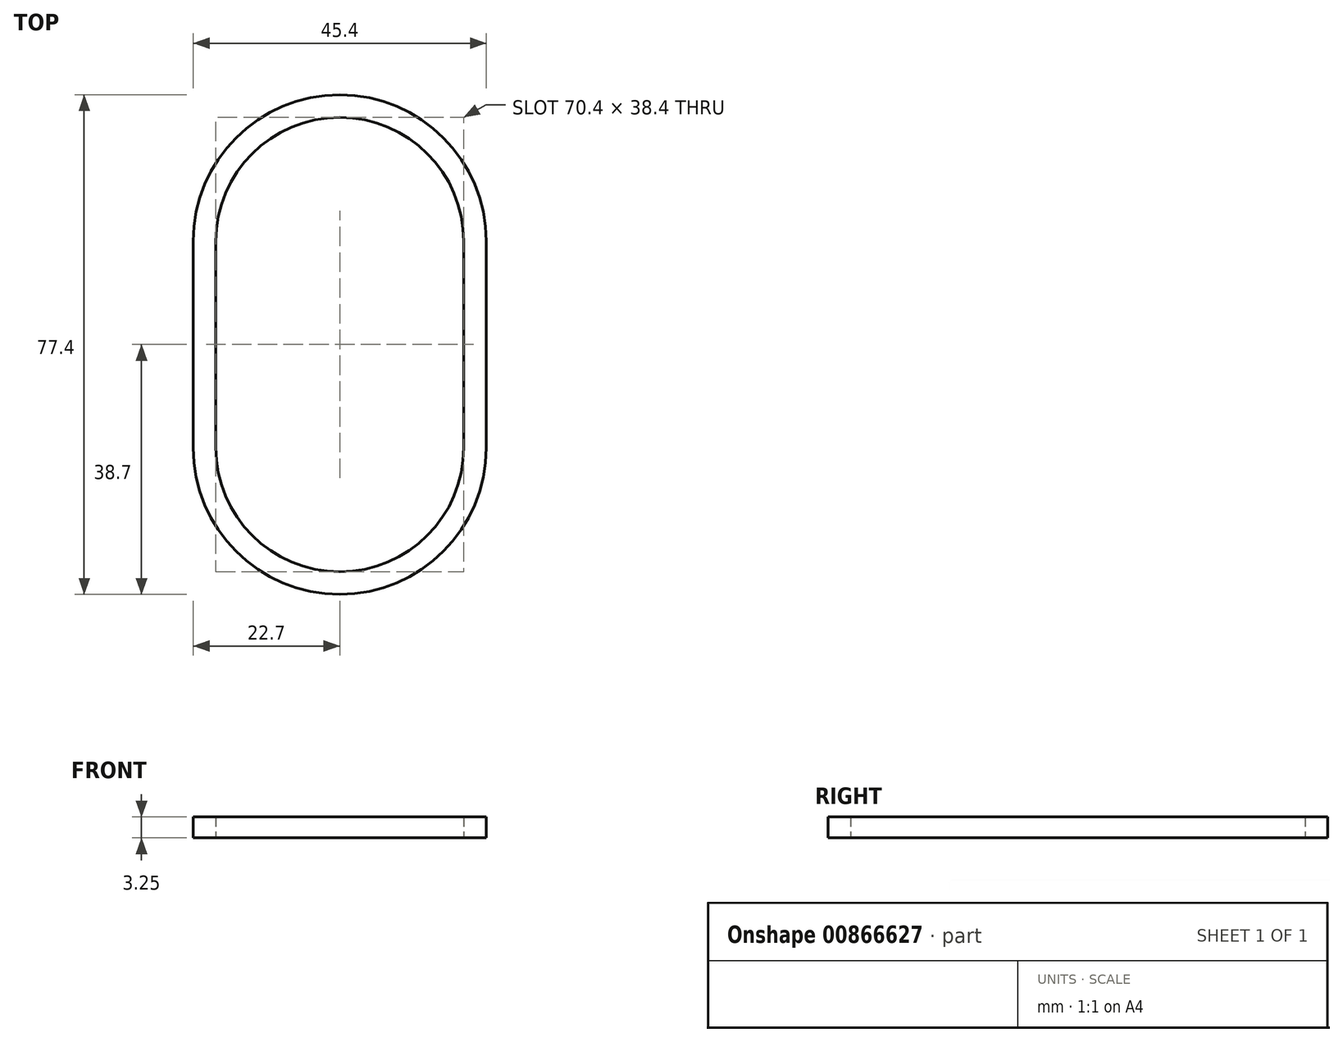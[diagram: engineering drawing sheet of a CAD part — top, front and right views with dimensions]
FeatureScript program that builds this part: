
annotation { "Feature Type Name" : "Feature", "Feature Type Description" : "" }
export const myFeature = defineFeature(function(context is Context, id is Id, definition is map)
    precondition{}
    {
        {
            var Q0;
            Q0=qCreatedBy(makeId("Top.planeOp"),FACE);
            var sketch = newSketch(context, id + "F0", { "sketchPlane" : qUnion([Q0])});
            skLineSegment(sketch, "E0", {"start": v(0, 0) * mm, "end": v(0, 38.75) * mm});
            skLineSegment(sketch, "E1", {"start": v(0, 0) * mm, "end": v(0, -38.75) * mm});
            skPoint(sketch, "E2", {"position": v(0, -16) * mm});
            skLineSegment(sketch, "E3", {"start": v(0, -16) * mm, "end": v(-22.75, -16) * mm});
            skLineSegment(sketch, "E4", {"start": v(0, -16) * mm, "end": v(22.75, -16) * mm});
            skPoint(sketch, "E5", {"position": v(0, 16) * mm});
            skLineSegment(sketch, "E6", {"start": v(0, 16) * mm, "end": v(-22.75, 16) * mm});
            skLineSegment(sketch, "E7", {"start": v(0, 16) * mm, "end": v(22.75, 16) * mm});
            skArc(sketch, "E8.0", {"start": v(22.7, 16) * mm, "mid": v(0, 38.7) * mm, "end": v(-22.7, 16) * mm});
            skLineSegment(sketch, "E8.1", {"start": v(22.7, -16) * mm, "end": v(22.7, 16) * mm});
            skArc(sketch, "E8.2", {"start": v(-22.7, -16) * mm, "mid": v(0, -38.7) * mm, "end": v(22.7, -16) * mm});
            skLineSegment(sketch, "E8.3", {"start": v(-22.7, 16) * mm, "end": v(-22.7, -16) * mm});
            skArc(sketch, "E9.0", {"start": v(19.2, 16) * mm, "mid": v(0, 35.2) * mm, "end": v(-19.2, 16) * mm});
            skLineSegment(sketch, "E9.1", {"start": v(19.2, -16) * mm, "end": v(19.2, 16) * mm});
            skArc(sketch, "E9.2", {"start": v(-19.2, -16) * mm, "mid": v(0, -35.2) * mm, "end": v(19.2, -16) * mm});
            skLineSegment(sketch, "E9.3", {"start": v(-19.2, 16) * mm, "end": v(-19.2, -16) * mm});
            skSolve(sketch);
        }
        {
            var Q0;
            {var subQ0=sQuery(id+"F0.wireOp",EDGE,"E8.0");var subQ1=sQuery(id+"F0.wireOp",EDGE,"E0");var subQ2=makeQuery(id+"F0.imprint","INTERSECT",VERTEX,{"derivedFrom":[subQ1,subQ0]});Q0=makeQuery(id+"F0.imprint","IMPRINT",FACE,{"disambiguationData":[TD([[makeQuery(id+"F0.imprint","IMPRINT",EDGE,{"disambiguationData":[TD([[subQ2,1.0]])],"derivedFrom":subQ1}),-1.0]])]});}
            var Q1;
            {var subQ0=sQuery(id+"F0.wireOp",EDGE,"E8.0");var subQ1=sQuery(id+"F0.wireOp",EDGE,"E0");var subQ2=makeQuery(id+"F0.imprint","INTERSECT",VERTEX,{"derivedFrom":[subQ1,subQ0]});Q1=makeQuery(id+"F0.imprint","IMPRINT",FACE,{"disambiguationData":[TD([[makeQuery(id+"F0.imprint","IMPRINT",EDGE,{"disambiguationData":[TD([[subQ2,1.0]])],"derivedFrom":subQ1}),1.0]])]});}
            var Q2;
            {var subQ0=sQuery(id+"F0.wireOp",EDGE,"E8.3");Q2=makeQuery(id+"F0.imprint","IMPRINT",FACE,{"disambiguationData":[TD([[makeQuery(id+"F0.imprint","IMPRINT",EDGE,{"derivedFrom":subQ0}),1.0]])]});}
            var Q3;
            {var subQ0=sQuery(id+"F0.wireOp",EDGE,"E8.2");var subQ1=sQuery(id+"F0.wireOp",EDGE,"E1");var subQ2=makeQuery(id+"F0.imprint","INTERSECT",VERTEX,{"derivedFrom":[subQ1,subQ0]});Q3=makeQuery(id+"F0.imprint","IMPRINT",FACE,{"disambiguationData":[TD([[makeQuery(id+"F0.imprint","IMPRINT",EDGE,{"disambiguationData":[TD([[subQ2,1.0]])],"derivedFrom":subQ1}),-1.0]])]});}
            var Q4;
            {var subQ0=sQuery(id+"F0.wireOp",EDGE,"E8.2");var subQ1=sQuery(id+"F0.wireOp",EDGE,"E1");var subQ2=makeQuery(id+"F0.imprint","INTERSECT",VERTEX,{"derivedFrom":[subQ1,subQ0]});Q4=makeQuery(id+"F0.imprint","IMPRINT",FACE,{"disambiguationData":[TD([[makeQuery(id+"F0.imprint","IMPRINT",EDGE,{"disambiguationData":[TD([[subQ2,1.0]])],"derivedFrom":subQ1}),1.0]])]});}
            var Q5;
            {var subQ0=sQuery(id+"F0.wireOp",EDGE,"E8.1");Q5=makeQuery(id+"F0.imprint","IMPRINT",FACE,{"disambiguationData":[TD([[makeQuery(id+"F0.imprint","IMPRINT",EDGE,{"derivedFrom":subQ0}),1.0]])]});}
            extrude(context, id + "F1", {"entities" : qUnion([Q0, Q1, Q2, Q3, Q4, Q5]), "depth" : 3.25 * mm, "offsetDistance" : 25 * mm});
        }
    });
